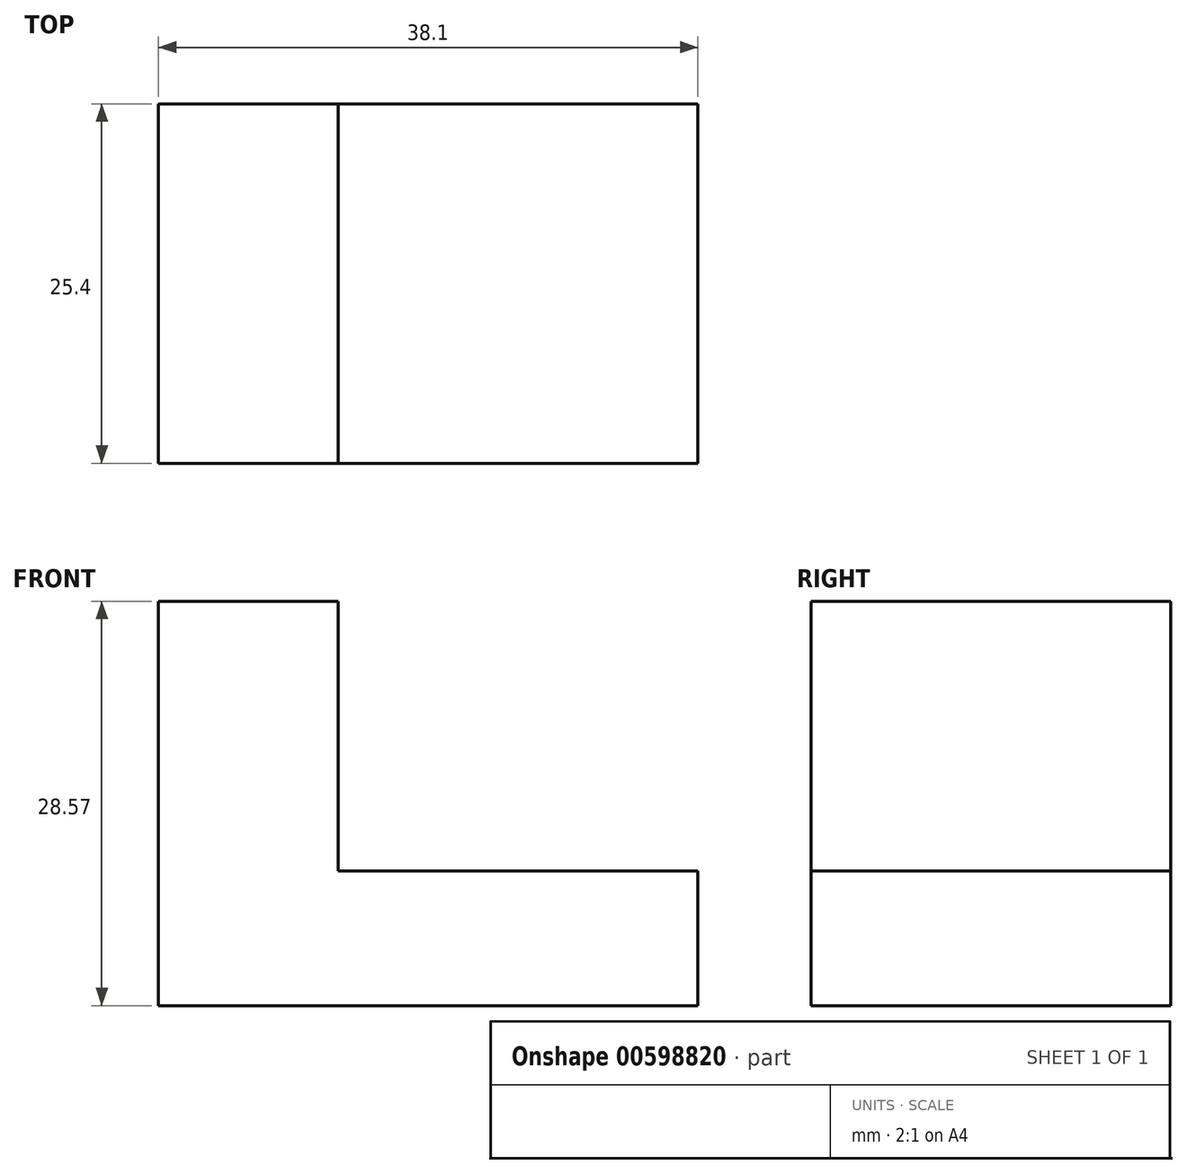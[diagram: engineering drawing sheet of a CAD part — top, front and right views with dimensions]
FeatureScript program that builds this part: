
annotation { "Feature Type Name" : "Feature", "Feature Type Description" : "" }
export const myFeature = defineFeature(function(context is Context, id is Id, definition is map)
    precondition{}
    {
        {
            var Q0;
            Q0=qCreatedBy(makeId("Front.planeOp"),FACE);
            var sketch = newSketch(context, id + "F0", { "sketchPlane" : qUnion([Q0])});
            skLineSegment(sketch, "E0", {"start": v(-23.85, -9.52) * mm, "end": v(14.25, -9.52) * mm});
            skLineSegment(sketch, "E1", {"start": v(-23.85, -9.52) * mm, "end": v(-23.85, 19.05) * mm});
            skLineSegment(sketch, "E2", {"start": v(-23.85, 19.05) * mm, "end": v(-11.15, 19.05) * mm});
            skLineSegment(sketch, "E3", {"start": v(-11.15, 19.05) * mm, "end": v(-11.15, 0) * mm});
            skLineSegment(sketch, "E4", {"start": v(-11.15, 0) * mm, "end": v(14.25, 0) * mm});
            skLineSegment(sketch, "E5", {"start": v(14.25, 0) * mm, "end": v(14.25, -9.52) * mm});
            skSolve(sketch);
        }
        {
            var Q0;
            Q0 = qSketchRegion(id + "F0", true);
            extrude(context, id + "F1", {"entities" : qUnion([Q0]), "depth" : 25.4 * mm, "offsetDistance" : 25.4 * mm});
        }
    });
